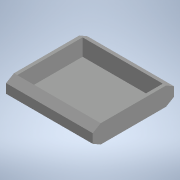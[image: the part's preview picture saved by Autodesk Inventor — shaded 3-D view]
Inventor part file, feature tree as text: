
AUTODESK INVENTOR PART (.ipt)
format: ipt  version: 2020 (Build 240168000, 168)  size: 121,344 bytes
history: native  units: in
note: dims shown in document units (in); Inventor stores cm internally (conversion verified against a paired STEP export)
features: extrude x2, sketch x2, projected_geometry x1
ambient origin geometry x8: Origin, YZ Plane, XZ Plane, XY Plane, X Axis, Y Axis, Z Axis, Center Point
bodies: Solid1 (feature_tree)
feature tree (5):
  extrude  "Extrusion1"  Depth=5.9055in
  extrude  "Extrusion2"  TaperAngle=0.0deg  [1 undecoded]
  sketch  "Sketch1"  dims[d0=1.3386in d1=5.9055in]
  sketch  "Sketch2"  dims[d2=6.2992in d3=0.0in d4=0.2362in d5=1.2205in d6=0.0in]
  projected_geometry  "Projected Loop1"
note: 1 required parameter value undecoded (feature->parameter linkage not recoverable at this tier; creation-order binding heuristic only, values carry confidence <= 0.55)
